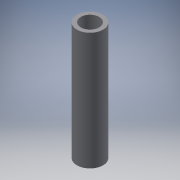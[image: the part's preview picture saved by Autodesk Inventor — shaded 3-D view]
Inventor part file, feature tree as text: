
AUTODESK INVENTOR PART (.ipt)
format: ipt  version: 2016 (Build 200138000, 138)  size: 92,672 bytes
history: native  units: mm
features: extrude x1, sketch x1
ambient origin geometry x8: Origin, YZ Plane, XZ Plane, XY Plane, X Axis, Y Axis, Z Axis, Center Point
bodies: Solid1 (feature_tree)
feature tree (2):
  extrude  "Extrusion1"  Depth=18.0mm
  sketch  "Sketch1"  dims[d0=4.0mm d1=2.8mm d2=18.0mm d3=0.0mm]
